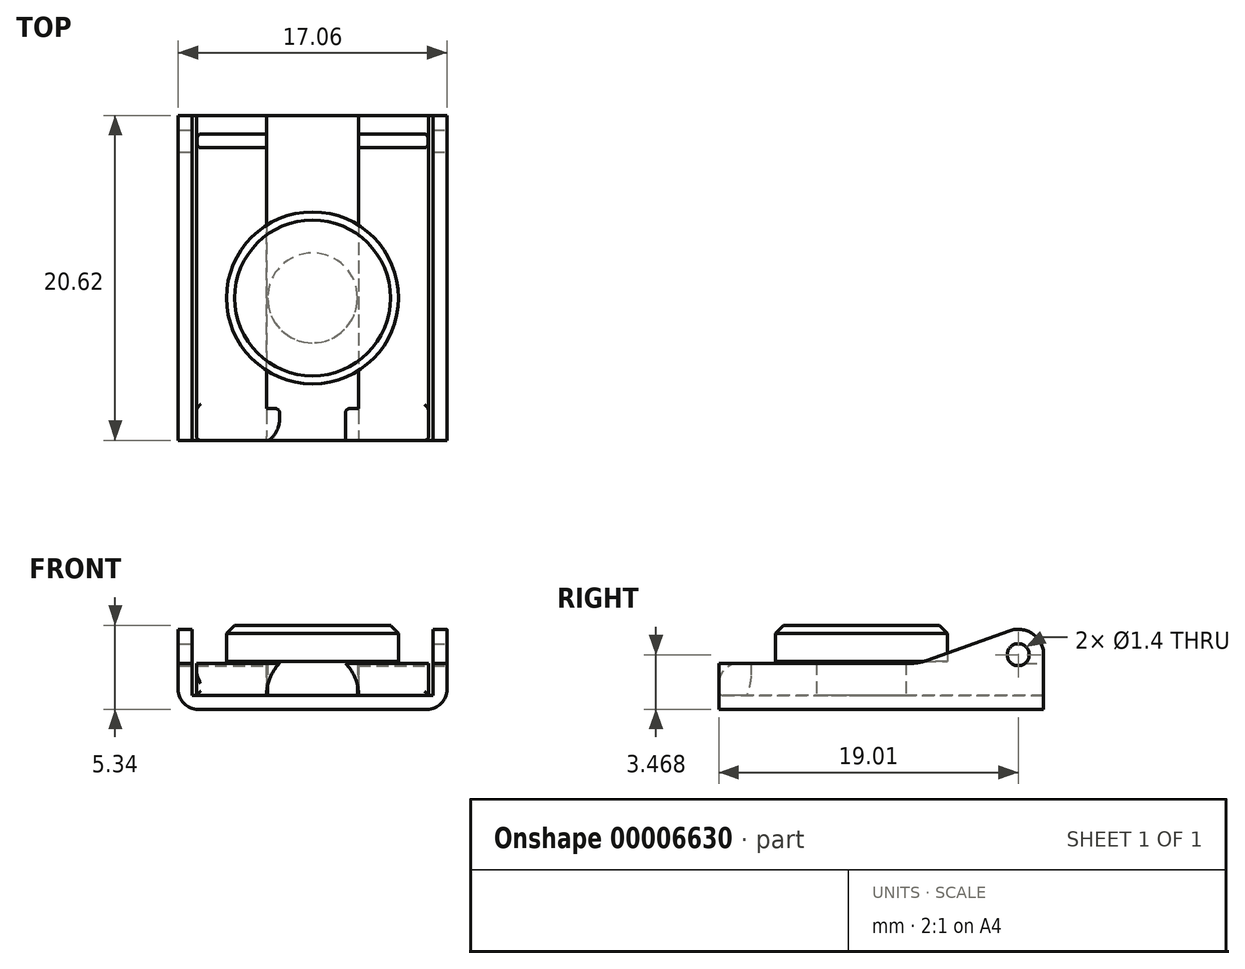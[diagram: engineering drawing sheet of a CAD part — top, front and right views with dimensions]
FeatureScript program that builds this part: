
annotation { "Feature Type Name" : "Feature", "Feature Type Description" : "" }
export const myFeature = defineFeature(function(context is Context, id is Id, definition is map)
    precondition{}
    {
        {
            var Q0;
            Q0=qCreatedBy(makeId("Right.planeOp"),FACE);
            var sketch = newSketch(context, id + "F0", { "sketchPlane" : qUnion([Q0])});
            skLineSegment(sketch, "E0", {"start": v(-2.03, 0) * mm, "end": v(35.43, 0) * mm});
            skLineSegment(sketch, "E1", {"start": v(35.43, 0) * mm, "end": v(35.43, 2.03) * mm});
            skLineSegment(sketch, "E2", {"start": v(35.43, 2.03) * mm, "end": v(0, 2.03) * mm});
            skLineSegment(sketch, "E3", {"start": v(0, 2.03) * mm, "end": v(0, 13.3) * mm});
            skLineSegment(sketch, "E4", {"start": v(0, 13.3) * mm, "end": v(-2.03, 13.3) * mm});
            skLineSegment(sketch, "E5", {"start": v(-2.03, 13.3) * mm, "end": v(-2.03, 0) * mm});
            skSolve(sketch);
        }
        {
            var Q0;
            Q0=makeQuery(id+"F0.imprint","IMPRINT",FACE,{"disambiguationData":[TD([[makeQuery(id+"F0.imprint","IMPRINT",EDGE,{"derivedFrom":sQuery(id+"F0.wireOp",EDGE,"E0")}),1.0]])]});
            extrude(context, id + "F1", {"entities" : qUnion([Q0]), "endBound" : BoundingType.SYMMETRIC, "depth" : 14.73 * mm});
        }
        {
            var Q0;
            Q0=makeQuery(id+"F1.opExtrude","SWEPT_FACE",FACE,{"disambiguationData":[OSD([sQuery(id+"F0.wireOp",EDGE,"E5")])]});
            var sketch = newSketch(context, id + "F2", { "sketchPlane" : qUnion([Q0])});
            skLineSegment(sketch, "E6", {"start": v(0, 20.06) * mm, "end": v(0, -10.13) * mm, "construction": true});
            skLineSegment(sketch, "E7", {"start": v(-11.93, 0) * mm, "end": v(7.65, 0) * mm, "construction": true});
            skLineSegment(sketch, "E8", {"start": v(-9.15, 13.3) * mm, "end": v(-7.37, 13.3) * mm, "construction": true});
            skLineSegment(sketch, "E9", {"start": v(-7.37, -1.71) * mm, "end": v(-7.37, 5.94) * mm, "construction": true});
            skLineSegment(sketch, "E10", {"start": v(7.37, 14.17) * mm, "end": v(7.37, 13.3) * mm, "construction": true});
            skLineSegment(sketch, "E11", {"start": v(-7.37, 13.7) * mm, "end": v(0, 13.7) * mm, "construction": true});
            skLineSegment(sketch, "E12", {"start": v(-9.15, 13.3) * mm, "end": v(-9.15, 5.94) * mm, "construction": true});
            skLineSegment(sketch, "E13", {"start": v(-11.04, 5.94) * mm, "end": v(10.31, 5.94) * mm, "construction": true});
            skArc(sketch, "E14", {"start": v(-4.35, 0) * mm, "mid": v(4.35, 11.89) * mm, "end": v(-4.35, 0) * mm});
            skCircle(sketch, "E15", {"center": v(0, 5.94) * mm, "radius": 2.03 * mm});
            skArc(sketch, "E16", {"start": v(2.92, 0) * mm, "mid": v(0, 2.92) * mm, "end": v(-2.92, 0) * mm});
            skLineSegment(sketch, "E17.trimOffspring", {"start": v(-7.37, 13.3) * mm, "end": v(-7.37, 14.6) * mm, "construction": true});
            skLineSegment(sketch, "E18.trimOffspring", {"start": v(7.37, 13.3) * mm, "end": v(9.58, 13.3) * mm, "construction": true});
            skLineSegment(sketch, "E19.trimOffspring", {"start": v(7.37, 5.94) * mm, "end": v(7.37, -2.08) * mm, "construction": true});
            skLineSegment(sketch, "E20", {"start": v(-7.37, 5.94) * mm, "end": v(-7.37, 0) * mm});
            skLineSegment(sketch, "E21", {"start": v(-7.37, 0) * mm, "end": v(-2.92, 0) * mm});
            skLineSegment(sketch, "E22", {"start": v(2.92, 0) * mm, "end": v(7.37, 0) * mm});
            skLineSegment(sketch, "E23", {"start": v(7.37, 0) * mm, "end": v(7.37, 5.94) * mm});
            skArc(sketch, "E24.trimOffspring", {"start": v(4.35, 0) * mm, "mid": v(-4.35, 11.89) * mm, "end": v(4.35, 0) * mm});
            skArc(sketch, "E25.trimOffspring", {"start": v(7.37, 5.94) * mm, "mid": v(0, 13.3) * mm, "end": v(-7.37, 5.94) * mm});
            skLineSegment(sketch, "E26", {"start": v(-7.37, 13.3) * mm, "end": v(-7.37, 13.3) * mm});
            skLineSegment(sketch, "E27", {"start": v(-7.37, 13.3) * mm, "end": v(7.37, 13.3) * mm});
            skLineSegment(sketch, "E28", {"start": v(7.37, 13.3) * mm, "end": v(7.37, 13.3) * mm});
            skLineSegment(sketch, "E29", {"start": v(-7.65, 0) * mm, "end": v(7.65, 0) * mm});
            skLineSegment(sketch, "E30", {"start": v(7.65, 4.7) * mm, "end": v(7.65, 0) * mm});
            skLineSegment(sketch, "E31", {"start": v(-8.53, -0.89) * mm, "end": v(8.53, -0.89) * mm});
            skLineSegment(sketch, "E32", {"start": v(8.53, 4.7) * mm, "end": v(8.53, -0.89) * mm});
            skLineSegment(sketch, "E33.0.MirrorCS", {"start": v(-7.65, 4.7) * mm, "end": v(-7.65, 0) * mm});
            skLineSegment(sketch, "E34.0.MirrorCS", {"start": v(-8.53, 4.7) * mm, "end": v(-8.53, -0.89) * mm});
            skLineSegment(sketch, "E35", {"start": v(-8.53, 4.7) * mm, "end": v(-7.65, 4.7) * mm});
            skLineSegment(sketch, "E36", {"start": v(7.65, 4.7) * mm, "end": v(8.53, 4.7) * mm});
            skPoint(sketch, "E37.orphan", {"position": v(-8.53, -2.35) * mm});
            skLineSegment(sketch, "E38.trimOffspring", {"start": v(-7.65, -0.89) * mm, "end": v(-7.65, -1.2) * mm});
            skPoint(sketch, "E39.orphan", {"position": v(-8.53, 0) * mm});
            skPoint(sketch, "E40.orphan", {"position": v(8.53, 0) * mm});
            skLineSegment(sketch, "E41.trimOffspring", {"start": v(8.53, 0) * mm, "end": v(17.06, 0) * mm, "construction": true});
            skPoint(sketch, "E42.trimOffspring.end.orphan", {"position": v(7.65, -1.2) * mm});
            skPoint(sketch, "E43.orphan", {"position": v(9.4, -0.89) * mm});
            skPoint(sketch, "E44.orphan", {"position": v(8.53, -2.35) * mm});
            skSolve(sketch);
        }
        {
            var Q0;
            {var subQ0=sQuery(id+"F0.wireOp",EDGE,"E5");var subQ2=sQuery(id+"F2.wireOp",EDGE,"E25.trimOffspring");var subQ4=makeQuery(id+"F1.opExtrude","CAP_EDGE",EDGE,{"disambiguationData":[OSD([subQ0])],"isStart":true});var subQ6=makeQuery(id+"F2.imprint","INTERSECT",VERTEX,{"derivedFrom":[subQ4,sQuery(id+"F2.wireOp",EDGE,"E20"),subQ2]});Q0=makeQuery(id+"F2.imprint","IMPRINT",FACE,{"disambiguationData":[TD([[makeQuery(id+"F2.imprint","IMPRINT",EDGE,{"disambiguationData":[TD([[subQ6,1.0]])],"derivedFrom":subQ2}),-1.0]])]});}
            var Q1;
            {var subQ0=sQuery(id+"F0.wireOp",EDGE,"E5");var subQ2=sQuery(id+"F2.wireOp",EDGE,"E25.trimOffspring");var subQ4=makeQuery(id+"F1.opExtrude","CAP_EDGE",EDGE,{"disambiguationData":[OSD([subQ0])],"isStart":false});var subQ6=makeQuery(id+"F2.imprint","INTERSECT",VERTEX,{"derivedFrom":[subQ4,sQuery(id+"F2.wireOp",EDGE,"E23"),subQ2]});Q1=makeQuery(id+"F2.imprint","IMPRINT",FACE,{"disambiguationData":[TD([[makeQuery(id+"F2.imprint","IMPRINT",EDGE,{"disambiguationData":[TD([[subQ6,-1.0]])],"derivedFrom":subQ2}),-1.0]])]});}
            var Q2;
            Q2=makeQuery(id+"F2.imprint","IMPRINT",FACE,{"disambiguationData":[TD([[makeQuery(id+"F2.imprint","IMPRINT",EDGE,{"derivedFrom":sQuery(id+"F2.wireOp",EDGE,"E15")}),1.0]])]});
            var Q3;
            {var subQ1=sQuery(id+"F2.wireOp",EDGE,"E16");Q3=makeQuery(id+"F2.imprint","IMPRINT",FACE,{"disambiguationData":[TD([[makeQuery(id+"F2.imprint","IMPRINT",EDGE,{"derivedFrom":subQ1}),1.0]])]});}
            var Q4;
            {var subQ4=sQuery(id+"F2.wireOp",EDGE,"E26");Q4=makeQuery(id+"F2.imprint","IMPRINT",FACE,{"disambiguationData":[TD([[makeQuery(id+"F2.imprint","IMPRINT",EDGE,{"derivedFrom":subQ4}),-1.0]])]});}
            extrude(context, id + "F3", {"entities" : qUnion([Q0, Q1, Q2, Q3, Q4]), "operationType" : NewBodyOperationType.REMOVE, "oppositeDirection" : true, "depth" : 2.54 * mm});
        }
        {
            var Q0;
            Q0=qCreatedBy(makeId("Top.planeOp"),FACE);
            var sketch = newSketch(context, id + "F4", { "sketchPlane" : qUnion([Q0])});
            skLineSegment(sketch, "E45.rect.bottom", {"start": v(2.92, 0) * mm, "end": v(-2.92, 0) * mm});
            skLineSegment(sketch, "E45.rect.left", {"start": v(2.92, 0) * mm, "end": v(2.92, 21) * mm});
            skLineSegment(sketch, "E45.rect.right", {"start": v(-2.92, 0) * mm, "end": v(-2.92, 21) * mm});
            skPoint(sketch, "E45.rect.middle", {"position": v(0, 10.5) * mm});
            skArc(sketch, "E46", {"start": v(-0.5, 23.88) * mm, "mid": v(-2.24, 22.88) * mm, "end": v(-2.92, 21) * mm});
            skLineSegment(sketch, "E47", {"start": v(8.78, 23.93) * mm, "end": v(-8.08, 23.93) * mm, "construction": true});
            skLineSegment(sketch, "E48", {"start": v(-8.55, 26) * mm, "end": v(8.78, 26) * mm, "construction": true});
            skArc(sketch, "E49", {"start": v(-2, 30.51) * mm, "mid": v(-2.55, 27.85) * mm, "end": v(-0.5, 26.06) * mm});
            skLineSegment(sketch, "E50", {"start": v(0.5, 26.06) * mm, "end": v(0.5, 23.88) * mm});
            skLineSegment(sketch, "E51", {"start": v(-0.5, 26.06) * mm, "end": v(-0.5, 23.88) * mm});
            skLineSegment(sketch, "E52", {"start": v(2, 30.51) * mm, "end": v(8.55, 36.47) * mm});
            skLineSegment(sketch, "E53", {"start": v(0, 28.7) * mm, "end": v(0, 37.53) * mm, "construction": true});
            skLineSegment(sketch, "E54.0.MirrorCS", {"start": v(-2, 30.51) * mm, "end": v(-8.55, 36.47) * mm});
            skLineSegment(sketch, "E55", {"start": v(-8.55, 36.47) * mm, "end": v(8.55, 36.47) * mm});
            skPoint(sketch, "E56.orphan", {"position": v(-0.5, 28.7) * mm});
            skPoint(sketch, "E57.orphan", {"position": v(0.5, 28.7) * mm});
            skArc(sketch, "E58.trimOffspring", {"start": v(0.5, 26.06) * mm, "mid": v(2.55, 27.85) * mm, "end": v(2, 30.51) * mm});
            skPoint(sketch, "E59.orphan", {"position": v(-0.5, 22.76) * mm});
            skPoint(sketch, "E60.orphan", {"position": v(0.5, 21) * mm});
            skArc(sketch, "E61.trimOffspring", {"start": v(2.92, 21) * mm, "mid": v(2.24, 22.88) * mm, "end": v(0.5, 23.88) * mm});
            skSolve(sketch);
        }
        {
            var Q0;
            Q0=makeQuery(id+"F4.imprint","IMPRINT",FACE,{"disambiguationData":[TD([[makeQuery(id+"F4.imprint","IMPRINT",EDGE,{"derivedFrom":sQuery(id+"F4.wireOp",EDGE,"E45.rect.bottom")}),-1.0]])]});
            extrude(context, id + "F5", {"entities" : qUnion([Q0]), "operationType" : NewBodyOperationType.REMOVE, "depth" : 2.08 * mm});
        }
        {
            var Q0;
            Q0=makeQuery(id+"F5.boolean.opBoolean","INTERSECT",EDGE,{"derivedFrom":[makeQuery(id+"F1.opExtrude","SWEPT_FACE",FACE,{"disambiguationData":[OSD([sQuery(id+"F0.wireOp",EDGE,"E2")])]}),makeQuery(id+"F5.opExtrude","SWEPT_FACE",FACE,{"disambiguationData":[OSD([sQuery(id+"F4.wireOp",EDGE,"E58.trimOffspring")])]})]});
            var Q1;
            Q1=makeQuery(id+"F5.boolean.opBoolean","INTERSECT",EDGE,{"derivedFrom":[makeQuery(id+"F1.opExtrude","SWEPT_FACE",FACE,{"disambiguationData":[OSD([sQuery(id+"F0.wireOp",EDGE,"E2")])]}),makeQuery(id+"F5.opExtrude","SWEPT_FACE",FACE,{"disambiguationData":[OSD([sQuery(id+"F4.wireOp",EDGE,"E49")])]})]});
            var Q2;
            Q2=makeQuery(id+"F5.boolean.opBoolean","INTERSECT",EDGE,{"derivedFrom":[makeQuery(id+"F1.opExtrude","SWEPT_FACE",FACE,{"disambiguationData":[OSD([sQuery(id+"F0.wireOp",EDGE,"E2")])]}),makeQuery(id+"F5.opExtrude","SWEPT_FACE",FACE,{"disambiguationData":[OSD([sQuery(id+"F4.wireOp",EDGE,"E50")])]})]});
            var Q3;
            Q3=makeQuery(id+"F5.boolean.opBoolean","INTERSECT",EDGE,{"derivedFrom":[makeQuery(id+"F1.opExtrude","SWEPT_FACE",FACE,{"disambiguationData":[OSD([sQuery(id+"F0.wireOp",EDGE,"E2")])]}),makeQuery(id+"F5.opExtrude","SWEPT_FACE",FACE,{"disambiguationData":[OSD([sQuery(id+"F4.wireOp",EDGE,"E51")])]})]});
            fillet(context, id + "F6", {"entities" : qUnion([Q0, Q1, Q2, Q3]), "radius" : 0.25 * mm, "tangentPropagation" : true, "allowEdgeOverflow" : false});
        }
        {
            var Q0;
            Q0=makeQuery(id+"F5.boolean.opBoolean","INTERSECT",EDGE,{"derivedFrom":[makeQuery(id+"F1.opExtrude","CAP_FACE",FACE,{"disambiguationData":[OSD([sQuery(id+"F0.wireOp",EDGE,"E0"),sQuery(id+"F0.wireOp",EDGE,"E1"),sQuery(id+"F0.wireOp",EDGE,"E2"),sQuery(id+"F0.wireOp",EDGE,"E3"),sQuery(id+"F0.wireOp",EDGE,"E4"),sQuery(id+"F0.wireOp",EDGE,"E5")])],"isStart":true}),makeQuery(id+"F5.opExtrude","SWEPT_FACE",FACE,{"disambiguationData":[OSD([sQuery(id+"F4.wireOp",EDGE,"E54.0.MirrorCS")])]})]});
            var Q1;
            Q1=makeQuery(id+"F5.boolean.opBoolean","INTERSECT",EDGE,{"derivedFrom":[makeQuery(id+"F1.opExtrude","CAP_FACE",FACE,{"disambiguationData":[OSD([sQuery(id+"F0.wireOp",EDGE,"E0"),sQuery(id+"F0.wireOp",EDGE,"E1"),sQuery(id+"F0.wireOp",EDGE,"E2"),sQuery(id+"F0.wireOp",EDGE,"E3"),sQuery(id+"F0.wireOp",EDGE,"E4"),sQuery(id+"F0.wireOp",EDGE,"E5")])],"isStart":false}),makeQuery(id+"F5.opExtrude","SWEPT_FACE",FACE,{"disambiguationData":[OSD([sQuery(id+"F4.wireOp",EDGE,"E52")])]})]});
            fillet(context, id + "F7", {"entities" : qUnion([Q0, Q1]), "radius" : 0.76 * mm, "tangentPropagation" : true, "allowEdgeOverflow" : false});
        }
        {
            var Q0;
            Q0=makeQuery(id+"F5.boolean.opBoolean","INTERSECT",EDGE,{"derivedFrom":[makeQuery(id+"F1.opExtrude","SWEPT_FACE",FACE,{"disambiguationData":[OSD([sQuery(id+"F0.wireOp",EDGE,"E2")])]}),makeQuery(id+"F5.opExtrude","SWEPT_FACE",FACE,{"disambiguationData":[OSD([sQuery(id+"F4.wireOp",EDGE,"E54.0.MirrorCS")])]})]});
            var Q1;
            Q1=makeQuery(id+"F5.boolean.opBoolean","INTERSECT",EDGE,{"derivedFrom":[makeQuery(id+"F1.opExtrude","SWEPT_FACE",FACE,{"disambiguationData":[OSD([sQuery(id+"F0.wireOp",EDGE,"E2")])]}),makeQuery(id+"F5.opExtrude","SWEPT_FACE",FACE,{"disambiguationData":[OSD([sQuery(id+"F4.wireOp",EDGE,"E52")])]})]});
            chamfer(context, id + "F8", {"entities" : qUnion([Q0, Q1]), "width" : 1.27 * mm});
        }
        {
            var Q0;
            {var subQ0=sQuery(id+"F2.wireOp",EDGE,"E25.trimOffspring");var subQ1=makeQuery(id+"F2.imprint","INTERSECT",VERTEX,{"derivedFrom":[subQ0,sQuery(id+"F2.wireOp",EDGE,"E27")]});Q0=makeQuery(id+"F3.boolean.opBoolean","INTERSECT",EDGE,{"derivedFrom":[makeQuery(id+"F1.opExtrude","SWEPT_FACE",FACE,{"disambiguationData":[OSD([sQuery(id+"F0.wireOp",EDGE,"E3")])]}),makeQuery(id+"F3.opExtrude","SWEPT_FACE",FACE,{"disambiguationData":[OSD([subQ0]),TDD([makeQuery(id+"F2.imprint","IMPRINT",EDGE,{"disambiguationData":[TD([[subQ1,1.0]])],"derivedFrom":subQ0})])]}),makeQuery(id+"F3.opExtrude","SWEPT_FACE",FACE,{"disambiguationData":[OSD([subQ0]),TDD([makeQuery(id+"F2.imprint","IMPRINT",EDGE,{"disambiguationData":[TD([[subQ1,-1.0]])],"derivedFrom":subQ0})])]})]});}
            var Q1;
            Q1=makeQuery(id+"F1.opExtrude","CAP_EDGE",EDGE,{"disambiguationData":[OSD([sQuery(id+"F0.wireOp",EDGE,"E3")])],"isStart":false});
            var Q2;
            Q2=makeQuery(id+"F1.opExtrude","CAP_EDGE",EDGE,{"disambiguationData":[OSD([sQuery(id+"F0.wireOp",EDGE,"E5")])],"isStart":false});
            var Q3;
            Q3=makeQuery(id+"F1.opExtrude","CAP_EDGE",EDGE,{"disambiguationData":[OSD([sQuery(id+"F0.wireOp",EDGE,"E3")])],"isStart":true});
            var Q4;
            Q4=makeQuery(id+"F1.opExtrude","CAP_EDGE",EDGE,{"disambiguationData":[OSD([sQuery(id+"F0.wireOp",EDGE,"E5")])],"isStart":true});
            var Q5;
            Q5=makeQuery(id+"F1.opExtrude","CAP_EDGE",EDGE,{"disambiguationData":[OSD([sQuery(id+"F0.wireOp",EDGE,"E2")])],"isStart":false});
            var Q6;
            Q6=makeQuery(id+"F1.opExtrude","CAP_EDGE",EDGE,{"disambiguationData":[OSD([sQuery(id+"F0.wireOp",EDGE,"E2")])],"isStart":true});
            var Q7;
            {var subQ0=sQuery(id+"F2.wireOp",EDGE,"E25.trimOffspring");var subQ1=makeQuery(id+"F2.imprint","INTERSECT",VERTEX,{"derivedFrom":[subQ0,sQuery(id+"F2.wireOp",EDGE,"E27")]});Q7=makeQuery(id+"F3.boolean.opBoolean","TWEAK_EDGE",EDGE,{"derivedFrom":[makeQuery(id+"F3.opExtrude","CAP_EDGE",EDGE,{"disambiguationData":[OSD([subQ0]),TDD([makeQuery(id+"F2.imprint","IMPRINT",EDGE,{"disambiguationData":[TD([[subQ1,1.0]])],"derivedFrom":subQ0})])],"isStart":true}),makeQuery(id+"F3.opExtrude","CAP_EDGE",EDGE,{"disambiguationData":[OSD([subQ0]),TDD([makeQuery(id+"F2.imprint","IMPRINT",EDGE,{"disambiguationData":[TD([[subQ1,-1.0]])],"derivedFrom":subQ0})])],"isStart":true})]});}
            var Q8;
            Q8=makeQuery(id+"F3.boolean.opBoolean","INTERSECT",EDGE,{"derivedFrom":[makeQuery(id+"F1.opExtrude","SWEPT_FACE",FACE,{"disambiguationData":[OSD([sQuery(id+"F0.wireOp",EDGE,"E3")])]}),makeQuery(id+"F3.opExtrude","SWEPT_FACE",FACE,{"disambiguationData":[OSD([sQuery(id+"F2.wireOp",EDGE,"E15")])]})]});
            var Q9;
            Q9=makeQuery(id+"F3.boolean.opBoolean","COPY",EDGE,{"derivedFrom":makeQuery(id+"F3.opExtrude","CAP_EDGE",EDGE,{"disambiguationData":[OSD([sQuery(id+"F2.wireOp",EDGE,"E15")])],"isStart":true})});
            var Q10;
            Q10=makeQuery(id+"F3.boolean.opBoolean","COPY",EDGE,{"derivedFrom":makeQuery(id+"F3.opExtrude","CAP_EDGE",EDGE,{"disambiguationData":[OSD([sQuery(id+"F2.wireOp",EDGE,"E16")])],"isStart":true})});
            var Q11;
            Q11=makeQuery(id+"F5.boolean.opBoolean","INTERSECT",EDGE,{"derivedFrom":[makeQuery(id+"F3.boolean.opBoolean","COPY",FACE,{"derivedFrom":makeQuery(id+"F3.opExtrude","SWEPT_FACE",FACE,{"disambiguationData":[OSD([sQuery(id+"F2.wireOp",EDGE,"E16")])]})}),makeQuery(id+"F5.opExtrude","SWEPT_FACE",FACE,{"disambiguationData":[OSD([sQuery(id+"F4.wireOp",EDGE,"E45.rect.bottom")])]})]});
            var Q12;
            {var subQ0=sQuery(id+"F0.wireOp",EDGE,"E2");var subQ1=sQuery(id+"F0.wireOp",EDGE,"E3");Q12=makeQuery(id+"F3.boolean.opBoolean","SPLIT",EDGE,{"disambiguationData":[TD([makeQuery(id+"F1.opExtrude","CAP_FACE",FACE,{"disambiguationData":[OSD([sQuery(id+"F0.wireOp",EDGE,"E0"),sQuery(id+"F0.wireOp",EDGE,"E1"),subQ0,subQ1,sQuery(id+"F0.wireOp",EDGE,"E4"),sQuery(id+"F0.wireOp",EDGE,"E5")])],"isStart":false})])],"derivedFrom":makeQuery(id+"F1.opExtrude","SWEPT_EDGE",EDGE,{"disambiguationData":[OSD([subQ0,subQ1])]})});}
            var Q13;
            {var subQ0=sQuery(id+"F0.wireOp",EDGE,"E2");var subQ1=sQuery(id+"F0.wireOp",EDGE,"E3");Q13=makeQuery(id+"F3.boolean.opBoolean","SPLIT",EDGE,{"disambiguationData":[TD([makeQuery(id+"F1.opExtrude","CAP_FACE",FACE,{"disambiguationData":[OSD([sQuery(id+"F0.wireOp",EDGE,"E0"),sQuery(id+"F0.wireOp",EDGE,"E1"),subQ0,subQ1,sQuery(id+"F0.wireOp",EDGE,"E4"),sQuery(id+"F0.wireOp",EDGE,"E5")])],"isStart":true})])],"derivedFrom":makeQuery(id+"F1.opExtrude","SWEPT_EDGE",EDGE,{"disambiguationData":[OSD([subQ0,subQ1])]})});}
            var Q14;
            {var subQ0=sQuery(id+"F0.wireOp",EDGE,"E0");var subQ1=sQuery(id+"F0.wireOp",EDGE,"E5");Q14=makeQuery(id+"F3.boolean.opBoolean","SPLIT",EDGE,{"disambiguationData":[TD([makeQuery(id+"F1.opExtrude","CAP_FACE",FACE,{"disambiguationData":[OSD([subQ0,sQuery(id+"F0.wireOp",EDGE,"E1"),sQuery(id+"F0.wireOp",EDGE,"E2"),sQuery(id+"F0.wireOp",EDGE,"E3"),sQuery(id+"F0.wireOp",EDGE,"E4"),subQ1])],"isStart":true})])],"derivedFrom":makeQuery(id+"F1.opExtrude","SWEPT_EDGE",EDGE,{"disambiguationData":[OSD([subQ0,subQ1])]})});}
            var Q15;
            {var subQ0=sQuery(id+"F0.wireOp",EDGE,"E0");var subQ1=sQuery(id+"F0.wireOp",EDGE,"E5");Q15=makeQuery(id+"F3.boolean.opBoolean","SPLIT",EDGE,{"disambiguationData":[TD([makeQuery(id+"F1.opExtrude","CAP_FACE",FACE,{"disambiguationData":[OSD([subQ0,sQuery(id+"F0.wireOp",EDGE,"E1"),sQuery(id+"F0.wireOp",EDGE,"E2"),sQuery(id+"F0.wireOp",EDGE,"E3"),sQuery(id+"F0.wireOp",EDGE,"E4"),subQ1])],"isStart":false})])],"derivedFrom":makeQuery(id+"F1.opExtrude","SWEPT_EDGE",EDGE,{"disambiguationData":[OSD([subQ0,subQ1])]})});}
            fillet(context, id + "F9", {"entities" : qUnion([Q0, Q1, Q2, Q3, Q4, Q5, Q6, Q7, Q8, Q9, Q10, Q11, Q12, Q13, Q14, Q15]), "radius" : 0.25 * mm, "allowEdgeOverflow" : false});
        }
        {
            var Q0;
            {var subQ5=sQuery(id+"F2.wireOp",EDGE,"E30");Q0=makeQuery(id+"F2.imprint","IMPRINT",FACE,{"disambiguationData":[TD([[makeQuery(id+"F2.imprint","IMPRINT",EDGE,{"derivedFrom":subQ5}),1.0]])]});}
            extrude(context, id + "F10", {"entities" : qUnion([Q0]), "oppositeDirection" : true, "depth" : 20.7 * mm});
        }
        {
            var Q0;
            Q0=makeQuery(id+"F10.opExtrude","SWEPT_FACE",FACE,{"disambiguationData":[OSD([sQuery(id+"F2.wireOp",EDGE,"E32")])]});
            var sketch = newSketch(context, id + "F11", { "sketchPlane" : qUnion([Q0])});
            skLineSegment(sketch, "E62", {"start": v(-2.03, -0.89) * mm, "end": v(18.6, -0.89) * mm});
            skLineSegment(sketch, "E63", {"start": v(-2.03, 2.03) * mm, "end": v(10.12, 2.03) * mm});
            skLineSegment(sketch, "E64", {"start": v(10.67, 2.08) * mm, "end": v(10.67, 2.03) * mm});
            skArc(sketch, "E65", {"start": v(18.6, 2.58) * mm, "mid": v(17.9, 3.9) * mm, "end": v(16.44, 4.1) * mm});
            skCircle(sketch, "E66", {"center": v(16.98, 2.58) * mm, "radius": 0.7 * mm});
            skLineSegment(sketch, "E67", {"start": v(-2.03, 2.03) * mm, "end": v(-2.03, -0.89) * mm});
            skPoint(sketch, "E68.orphan", {"position": v(-2.75, 2.03) * mm});
            skPoint(sketch, "E69.orphan", {"position": v(-2.5, -0.89) * mm});
            skLineSegment(sketch, "E70", {"start": v(11.19, 2.22) * mm, "end": v(16.44, 4.1) * mm});
            skLineSegment(sketch, "E71.trimOffspring", {"start": v(18.6, 2.58) * mm, "end": v(18.6, -0.89) * mm});
            skPoint(sketch, "E72.orphan", {"position": v(18.6, -2.53) * mm});
            skPoint(sketch, "E73.start.orphan", {"position": v(-3.43, 4.2) * mm});
            skPoint(sketch, "E74.visualSharp", {"position": v(10.67, 2.03) * mm});
            skArc(sketch, "E74.filletArc", {"start": v(10.12, 2.03) * mm, "mid": v(10.66, 2.08) * mm, "end": v(11.19, 2.22) * mm});
            skPoint(sketch, "E75.trimOffspring.end.orphan", {"position": v(10.67, -3.2) * mm});
            skSolve(sketch);
        }
        {
            var Q0;
            Q0=makeQuery(id+"F11.imprint","IMPRINT",FACE,{"disambiguationData":[TD([[makeQuery(id+"F11.imprint","IMPRINT",EDGE,{"derivedFrom":sQuery(id+"F11.wireOp",EDGE,"E62")}),-1.0]])]});
            extrude(context, id + "F12", {"entities" : qUnion([Q0]), "operationType" : NewBodyOperationType.INTERSECT, "oppositeDirection" : true, "depth" : 17.78 * mm});
        }
        {
            var Q0;
            Q0=makeQuery(id+"F10.opExtrude","SWEPT_EDGE",EDGE,{"disambiguationData":[OSD([sQuery(id+"F2.wireOp",EDGE,"E31"),sQuery(id+"F2.wireOp",EDGE,"E34.0.MirrorCS")])]});
            var Q1;
            Q1=makeQuery(id+"F10.opExtrude","SWEPT_EDGE",EDGE,{"disambiguationData":[OSD([sQuery(id+"F2.wireOp",EDGE,"E31"),sQuery(id+"F2.wireOp",EDGE,"E32")])]});
            var Q2;
            Q2=makeQuery(id+"F12.boolean.opBoolean","COPY",EDGE,{"disambiguationData":[OD(0.0)],"derivedFrom":makeQuery(id+"F12.opExtrude","SWEPT_EDGE",EDGE,{"disambiguationData":[OSD([sQuery(id+"F2.wireOp",EDGE,"E32"),sQuery(id+"F11.wireOp",EDGE,"E63"),sQuery(id+"F11.wireOp",EDGE,"E67")])]})});
            var Q3;
            Q3=makeQuery(id+"F12.boolean.opBoolean","COPY",EDGE,{"disambiguationData":[OD(1.0)],"derivedFrom":makeQuery(id+"F12.opExtrude","SWEPT_EDGE",EDGE,{"disambiguationData":[OSD([sQuery(id+"F2.wireOp",EDGE,"E32"),sQuery(id+"F11.wireOp",EDGE,"E63"),sQuery(id+"F11.wireOp",EDGE,"E67")])]})});
            fillet(context, id + "F13", {"entities" : qUnion([Q0, Q1, Q2, Q3]), "radius" : 1.27 * mm, "allowEdgeOverflow" : false});
        }
        {
            var Q0;
            Q0=qCreatedBy(makeId("Top.planeOp"),FACE);
            var sketch = newSketch(context, id + "F14", { "sketchPlane" : qUnion([Q0])});
            skCircle(sketch, "E76", {"center": v(0, 7.01) * mm, "radius": 1.59 * mm});
            skCircle(sketch, "E77", {"center": v(0, 7.01) * mm, "radius": 2.85 * mm});
            skSolve(sketch);
        }
        {
            var Q0;
            Q0=makeQuery(id+"F14.imprint","IMPRINT",FACE,{"disambiguationData":[TD([[makeQuery(id+"F14.imprint","IMPRINT",EDGE,{"derivedFrom":sQuery(id+"F14.wireOp",EDGE,"E76")}),1.0]])]});
            extrude(context, id + "F15", {"entities" : qUnion([Q0]), "operationType" : NewBodyOperationType.REMOVE, "oppositeDirection" : true, "depth" : 1.02 * mm});
        }
        {
            var Q0;
            Q0=makeQuery(id+"F14.imprint","IMPRINT",FACE,{"disambiguationData":[TD([[makeQuery(id+"F14.imprint","IMPRINT",EDGE,{"derivedFrom":sQuery(id+"F14.wireOp",EDGE,"E76")}),1.0]])]});
            extrude(context, id + "F16", {"entities" : qUnion([Q0]), "oppositeDirection" : true, "depth" : 0.89 * mm});
        }
        {
            var Q0;
            Q0=makeQuery(id+"F14.imprint","IMPRINT",FACE,{"disambiguationData":[TD([[makeQuery(id+"F14.imprint","IMPRINT",EDGE,{"derivedFrom":sQuery(id+"F14.wireOp",EDGE,"E76")}),-1.0]])]});
            var Q1;
            Q1=makeQuery(id+"F14.imprint","IMPRINT",FACE,{"disambiguationData":[TD([[makeQuery(id+"F14.imprint","IMPRINT",EDGE,{"derivedFrom":sQuery(id+"F14.wireOp",EDGE,"E76")}),1.0]])]});
            extrude(context, id + "F17", {"entities" : qUnion([Q0, Q1]), "operationType" : NewBodyOperationType.ADD, "depth" : 2.16 * mm});
        }
        {
            var Q0;
            Q0=makeQuery(id+"F17.opExtrude","CAP_FACE",FACE,{"disambiguationData":[OSD([sQuery(id+"F14.wireOp",EDGE,"E77")])],"isStart":false});
            var sketch = newSketch(context, id + "F18", { "sketchPlane" : qUnion([Q0])});
            skCircle(sketch, "E78", {"center": v(0, 7.01) * mm, "radius": 5.46 * mm});
            skSolve(sketch);
        }
        {
            var Q0;
            Q0=makeQuery(id+"F18.imprint","IMPRINT",FACE,{"disambiguationData":[TD([[makeQuery(id+"F18.imprint","IMPRINT",EDGE,{"derivedFrom":makeQuery(id+"F17.opExtrude","CAP_EDGE",EDGE,{"disambiguationData":[OSD([sQuery(id+"F14.wireOp",EDGE,"E77")])],"isStart":false})}),1.0]])]});
            var Q1;
            Q1=makeQuery(id+"F18.imprint","IMPRINT",FACE,{"disambiguationData":[TD([[makeQuery(id+"F18.imprint","IMPRINT",EDGE,{"derivedFrom":sQuery(id+"F18.wireOp",EDGE,"E78")}),1.0]])]});
            extrude(context, id + "F19", {"entities" : qUnion([Q0, Q1]), "operationType" : NewBodyOperationType.ADD, "depth" : 2.3 * mm});
        }
        {
            var Q0;
            Q0=makeQuery(id+"F19.opExtrude","CAP_EDGE",EDGE,{"disambiguationData":[OSD([sQuery(id+"F18.wireOp",EDGE,"E78")])],"isStart":false});
            chamfer(context, id + "F20", {"entities" : qUnion([Q0]), "width" : 0.5 * mm, "tangentPropagation" : true});
        }
    });
